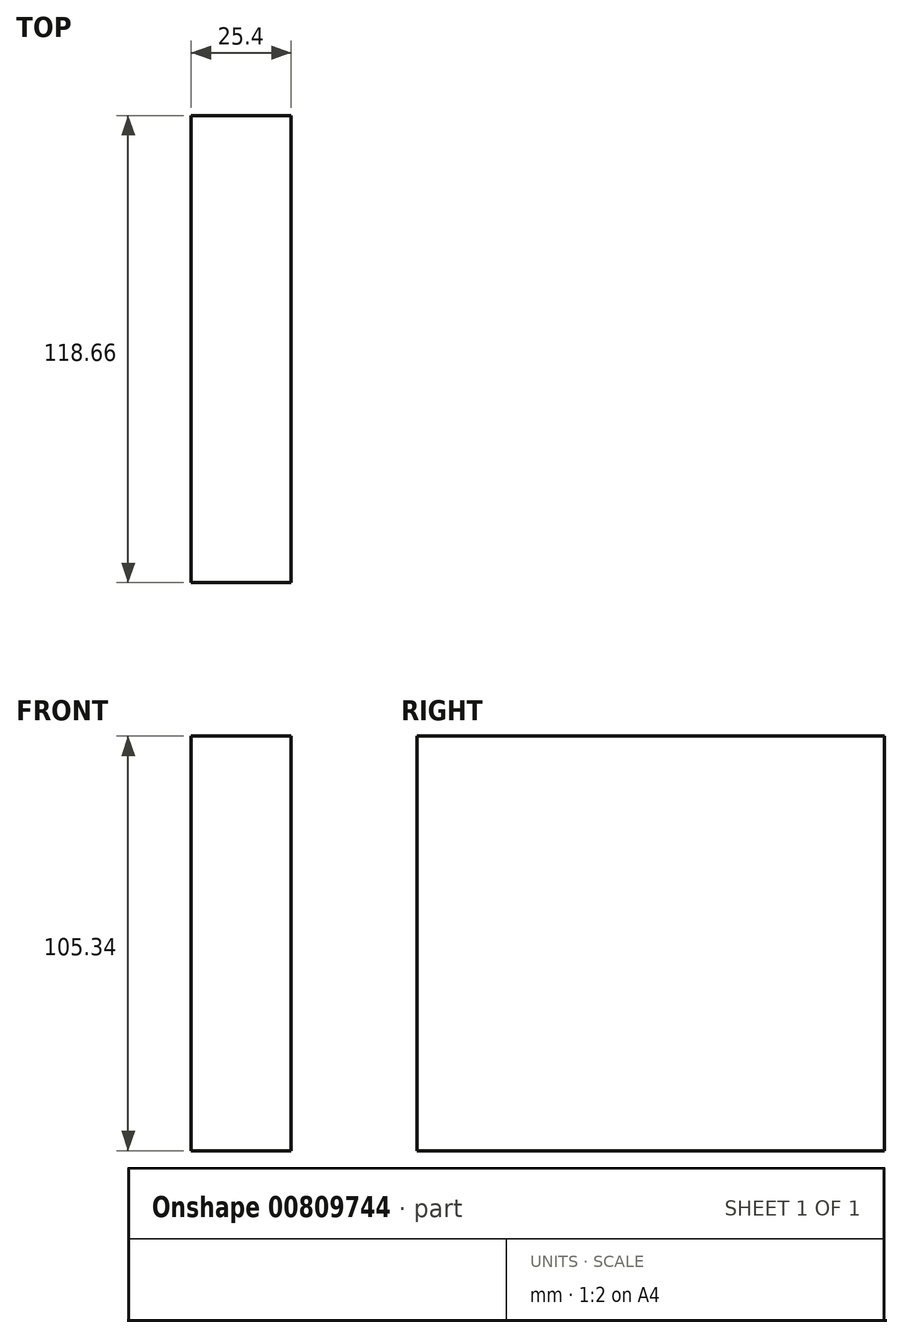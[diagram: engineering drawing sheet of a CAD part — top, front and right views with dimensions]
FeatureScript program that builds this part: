
annotation { "Feature Type Name" : "Feature", "Feature Type Description" : "" }
export const myFeature = defineFeature(function(context is Context, id is Id, definition is map)
    precondition{}
    {
        {
            var Q0;
            Q0=qCreatedBy(makeId("Right.planeOp"),FACE);
            var sketch = newSketch(context, id + "F0", { "sketchPlane" : qUnion([Q0])});
            skLineSegment(sketch, "E0.bottom", {"start": v(0, 0) * mm, "end": v(118.66, 0) * mm});
            skLineSegment(sketch, "E0.top", {"start": v(0, -105.34) * mm, "end": v(118.66, -105.34) * mm});
            skLineSegment(sketch, "E0.left", {"start": v(0, 0) * mm, "end": v(0, -105.34) * mm});
            skLineSegment(sketch, "E0.right", {"start": v(118.66, 0) * mm, "end": v(118.66, -105.34) * mm});
            skSolve(sketch);
        }
        {
            var Q0;
            Q0=makeQuery(id+"F0.imprint","IMPRINT",FACE,{"disambiguationData":[TD([[makeQuery(id+"F0.imprint","IMPRINT",EDGE,{"derivedFrom":sQuery(id+"F0.wireOp",EDGE,"E0.bottom")}),-1.0]])]});
            extrude(context, id + "F1", {"entities" : qUnion([Q0]), "depth" : 25.4 * mm, "offsetDistance" : 25.4 * mm});
        }
    });
